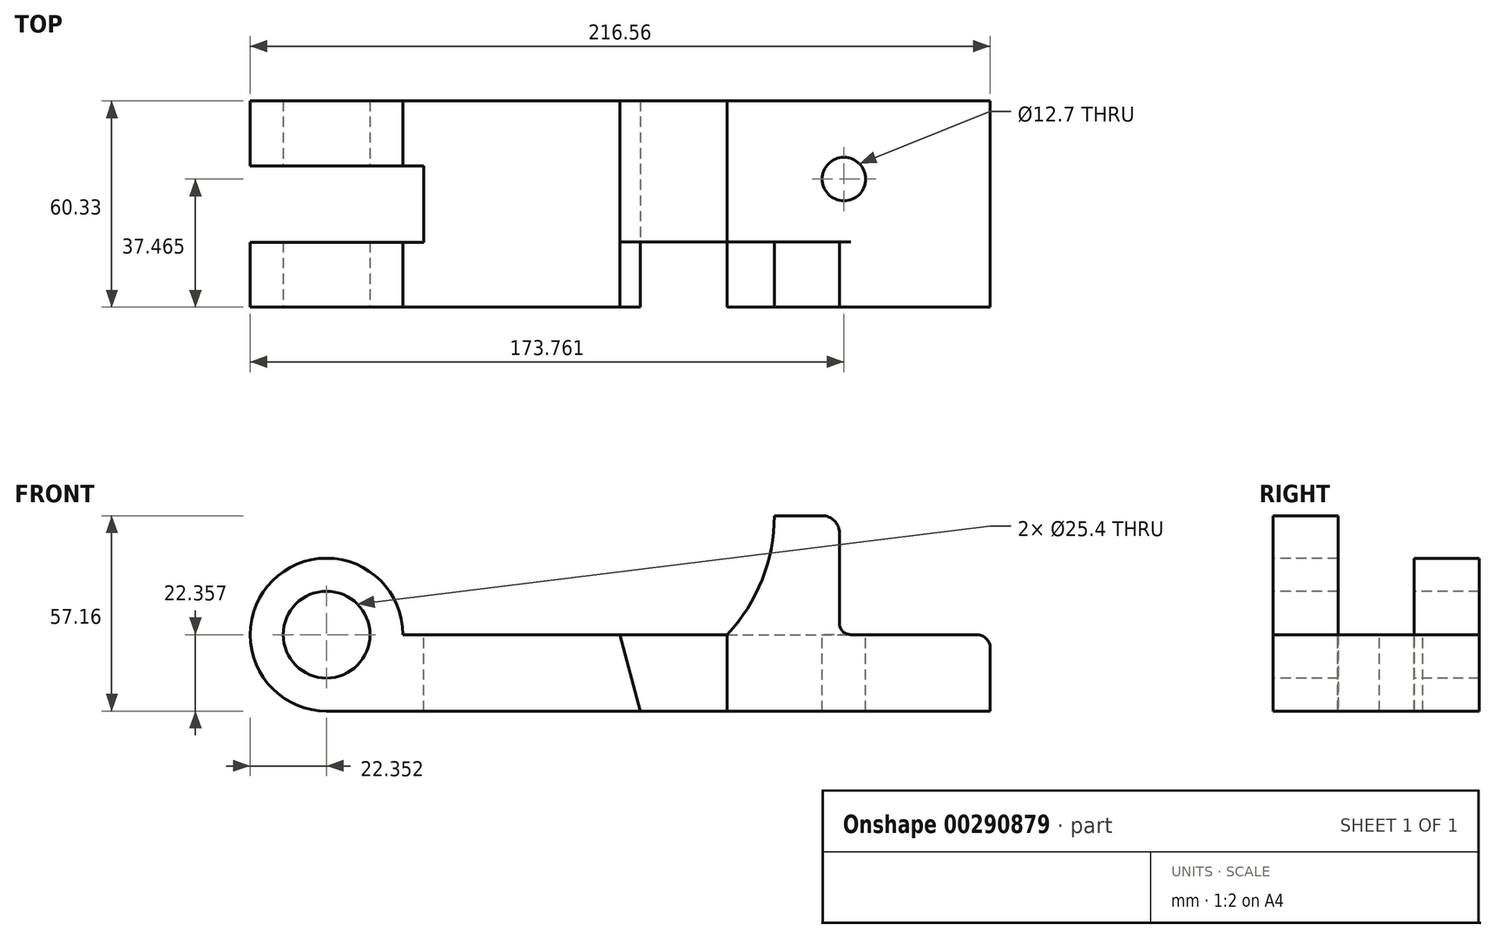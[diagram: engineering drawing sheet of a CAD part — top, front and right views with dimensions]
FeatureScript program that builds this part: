
annotation { "Feature Type Name" : "Feature", "Feature Type Description" : "" }
export const myFeature = defineFeature(function(context is Context, id is Id, definition is map)
    precondition{}
    {
        {
            var Q0;
            Q0=qCreatedBy(makeId("Front.planeOp"),FACE);
            var sketch = newSketch(context, id + "F0", { "sketchPlane" : qUnion([Q0])});
            skLineSegment(sketch, "E0.top", {"start": v(108.28, -28.58) * mm, "end": v(-85.93, -28.58) * mm});
            skPoint(sketch, "E0.middle", {"position": v(0, 0) * mm});
            skLineSegment(sketch, "E1", {"start": v(104.34, -6.22) * mm, "end": v(67.46, -6.22) * mm});
            skCircle(sketch, "E2", {"center": v(-85.93, -6.22) * mm, "radius": 12.7 * mm});
            skArc(sketch, "E3", {"start": v(-63.58, -6.22) * mm, "mid": v(-101.73, 9.58) * mm, "end": v(-85.93, -28.58) * mm});
            skPoint(sketch, "E4.orphan", {"position": v(-108.28, -28.58) * mm});
            skArc(sketch, "E5", {"start": v(108.28, -10.16) * mm, "mid": v(107.13, -7.38) * mm, "end": v(104.34, -6.22) * mm});
            skLineSegment(sketch, "E6", {"start": v(64.16, -2.92) * mm, "end": v(64.16, 23.5) * mm});
            skLineSegment(sketch, "E7", {"start": v(45.11, 28.57) * mm, "end": v(59.08, 28.57) * mm});
            skArc(sketch, "E8", {"start": v(64.16, 23.5) * mm, "mid": v(62.67, 27.09) * mm, "end": v(59.08, 28.57) * mm});
            skPoint(sketch, "E9.orphan", {"position": v(64.16, 28.57) * mm});
            skPoint(sketch, "E10.second.point", {"position": v(-56.48, 28.57) * mm});
            skPoint(sketch, "E10.third.point", {"position": v(-5.91, 80.12) * mm});
            skLineSegment(sketch, "E11.trimOffspring", {"start": v(31.32, -6.22) * mm, "end": v(-63.58, -6.22) * mm});
            skLineSegment(sketch, "E12", {"start": v(108.28, -10.16) * mm, "end": v(108.28, -28.58) * mm});
            skLineSegment(sketch, "E13", {"start": v(-0.08, -6.22) * mm, "end": v(5.92, -28.58) * mm});
            skLineSegment(sketch, "E14", {"start": v(-85.93, -6.22) * mm, "end": v(-108.28, -6.22) * mm, "construction": true});
            skLineSegment(sketch, "E15", {"start": v(31.32, -6.22) * mm, "end": v(31.32, -28.57) * mm});
            skArc(sketch, "E16", {"start": v(31.32, -6.22) * mm, "mid": v(41.54, 9.86) * mm, "end": v(45.11, 28.57) * mm});
            skArc(sketch, "E17", {"start": v(64.16, -2.92) * mm, "mid": v(65.13, -5.26) * mm, "end": v(67.46, -6.22) * mm});
            skLineSegment(sketch, "E18", {"start": v(31.32, -6.22) * mm, "end": v(67.46, -6.22) * mm});
            skSolve(sketch);
        }
        {
            var Q0;
            Q0=makeQuery(id+"F0.imprint","IMPRINT",FACE,{"disambiguationData":[TD([[makeQuery(id+"F0.imprint","IMPRINT",EDGE,{"derivedFrom":sQuery(id+"F0.wireOp",EDGE,"E1")}),1.0]])]});
            extrude(context, id + "F1", {"entities" : qUnion([Q0]), "oppositeDirection" : true, "depth" : 60.32 * mm});
        }
        {
            var Q0;
            Q0=makeQuery(id+"F0.imprint","IMPRINT",FACE,{"disambiguationData":[TD([[makeQuery(id+"F0.imprint","IMPRINT",EDGE,{"derivedFrom":sQuery(id+"F0.wireOp",EDGE,"E6")}),1.0]])]});
            extrude(context, id + "F2", {"entities" : qUnion([Q0]), "operationType" : NewBodyOperationType.ADD, "oppositeDirection" : true, "depth" : 19.05 * mm});
        }
        {
            var Q0;
            Q0=makeQuery(id+"F0.imprint","IMPRINT",FACE,{"disambiguationData":[TD([[makeQuery(id+"F0.imprint","IMPRINT",EDGE,{"derivedFrom":sQuery(id+"F0.wireOp",EDGE,"E2")}),-1.0]])]});
            extrude(context, id + "F3", {"entities" : qUnion([Q0]), "oppositeDirection" : true, "depth" : 60.32 * mm});
        }
        {
            var Q0;
            {var subQ0=sQuery(id+"F0.wireOp",EDGE,"E13");Q0=makeQuery(id+"F0.imprint","IMPRINT",FACE,{"disambiguationData":[TD([[makeQuery(id+"F0.imprint","IMPRINT",EDGE,{"derivedFrom":subQ0}),1.0]])]});}
            extrude(context, id + "F4", {"entities" : qUnion([Q0]), "oppositeDirection" : true, "depth" : 60.32 * mm});
        }
        {
            var Q0;
            {var subQ0=sQuery(id+"F0.wireOp",EDGE,"E13");Q0=makeQuery(id+"F0.imprint","IMPRINT",FACE,{"disambiguationData":[TD([[makeQuery(id+"F0.imprint","IMPRINT",EDGE,{"derivedFrom":subQ0}),1.0]])]});}
            extrude(context, id + "F5", {"entities" : qUnion([Q0]), "operationType" : NewBodyOperationType.REMOVE, "oppositeDirection" : true, "depth" : 19.05 * mm});
        }
        {
            var Q0;
            Q0=makeQuery(id+"F3.opExtrude","SWEPT_FACE",FACE,{"disambiguationData":[OSD([sQuery(id+"F0.wireOp",EDGE,"E11.trimOffspring")])]});
            var sketch = newSketch(context, id + "F6", { "sketchPlane" : qUnion([Q0])});
            skLineSegment(sketch, "E19.bottom", {"start": v(-119.37, 41.33) * mm, "end": v(-57.5, 41.33) * mm});
            skLineSegment(sketch, "E19.top", {"start": v(-119.37, 19) * mm, "end": v(-57.5, 19) * mm});
            skLineSegment(sketch, "E19.left", {"start": v(-119.37, 41.33) * mm, "end": v(-119.37, 19) * mm});
            skPoint(sketch, "E19.middle", {"position": v(-31.83, 30.16) * mm});
            skPoint(sketch, "E19.right.start.orphan", {"position": v(55.72, 41.33) * mm});
            skPoint(sketch, "E20.orphan", {"position": v(55.72, 19) * mm});
            skLineSegment(sketch, "E21", {"start": v(-57.5, 41.33) * mm, "end": v(-57.5, 19) * mm});
            skSolve(sketch);
        }
        {
            var Q0;
            {var subQ0=sQuery(id+"F6.wireOp",EDGE,"E21");Q0=makeQuery(id+"F6.imprint","IMPRINT",FACE,{"disambiguationData":[TD([[makeQuery(id+"F6.imprint","IMPRINT",EDGE,{"derivedFrom":subQ0}),-1.0]])]});}
            var Q1;
            {var subQ0=sQuery(id+"F6.wireOp",EDGE,"E19.left");Q1=makeQuery(id+"F6.imprint","IMPRINT",FACE,{"disambiguationData":[TD([[makeQuery(id+"F6.imprint","IMPRINT",EDGE,{"derivedFrom":subQ0}),1.0]])]});}
            extrude(context, id + "F7", {"entities" : qUnion([Q0, Q1]), "operationType" : NewBodyOperationType.REMOVE, "endBound" : BoundingType.SYMMETRIC, "oppositeDirection" : true, "depth" : 210.82 * mm});
        }
        {
            var Q0;
            Q0=makeQuery(id+"F1.opExtrude","SWEPT_FACE",FACE,{"disambiguationData":[OSD([sQuery(id+"F0.wireOp",EDGE,"E1"),sQuery(id+"F0.wireOp",EDGE,"E18")])]});
            var sketch = newSketch(context, id + "F8", { "sketchPlane" : qUnion([Q0])});
            skCircle(sketch, "E22", {"center": v(65.48, 37.46) * mm, "radius": 6.35 * mm});
            skSolve(sketch);
        }
        {
            var Q0;
            Q0=makeQuery(id+"F8.imprint","IMPRINT",FACE,{"disambiguationData":[TD([[makeQuery(id+"F8.imprint","IMPRINT",EDGE,{"derivedFrom":sQuery(id+"F8.wireOp",EDGE,"E22")}),1.0]])]});
            extrude(context, id + "F9", {"entities" : qUnion([Q0]), "operationType" : NewBodyOperationType.REMOVE, "endBound" : BoundingType.THROUGH_ALL, "oppositeDirection" : true, "depth" : 25.4 * mm});
        }
    });
